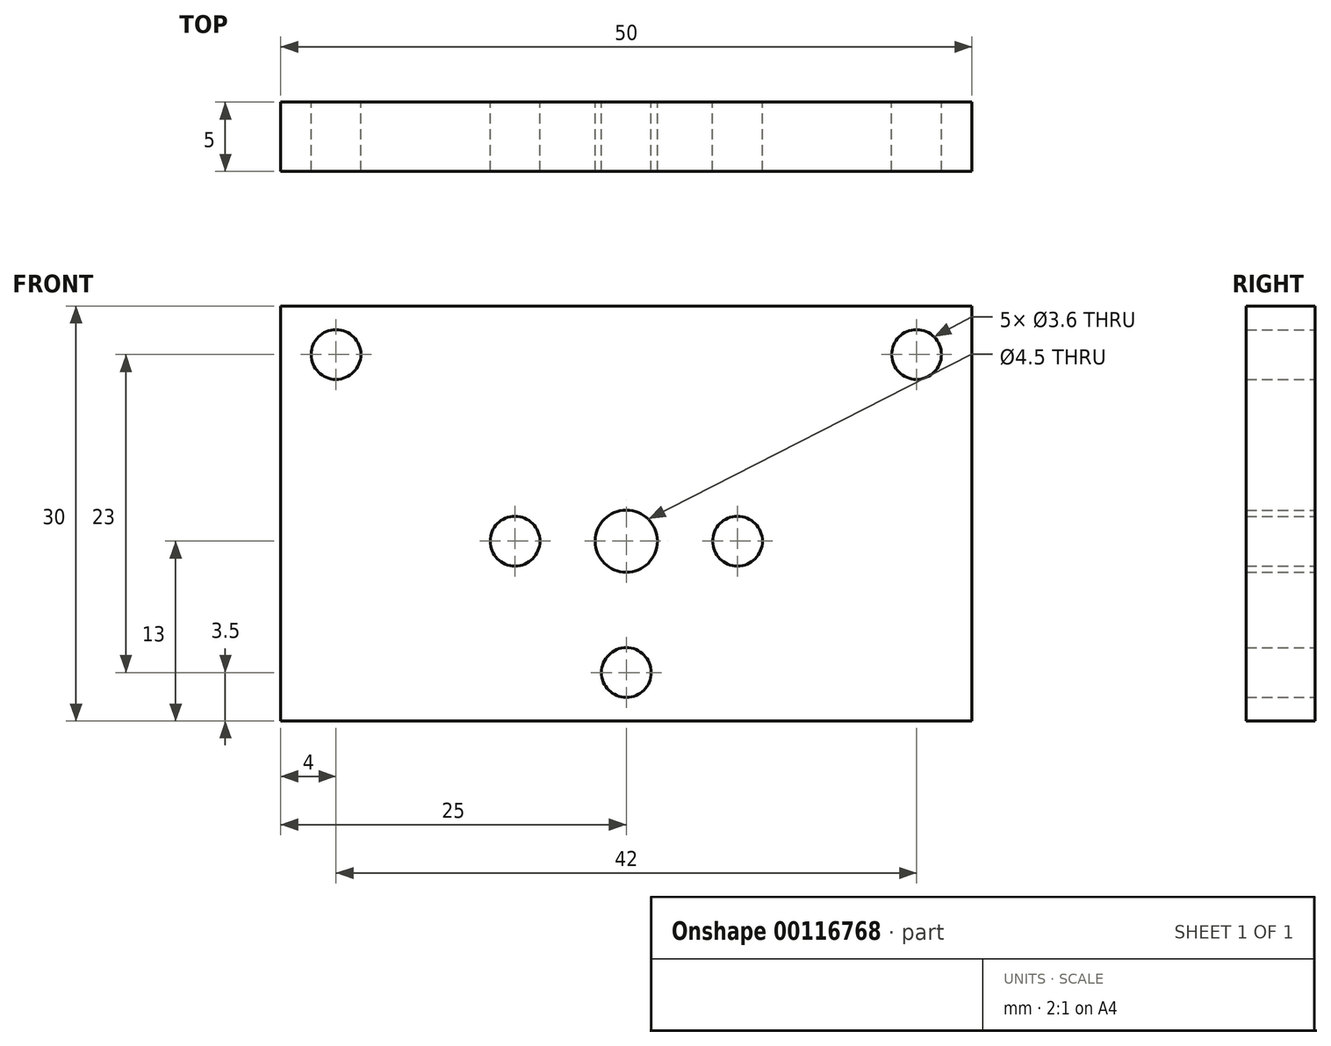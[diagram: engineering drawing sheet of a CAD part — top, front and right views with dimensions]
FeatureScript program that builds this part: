
annotation { "Feature Type Name" : "Feature", "Feature Type Description" : "" }
export const myFeature = defineFeature(function(context is Context, id is Id, definition is map)
    precondition{}
    {
        {
            var Q0;
            Q0=qCreatedBy(makeId("Front.planeOp"),FACE);
            var sketch = newSketch(context, id + "F0", { "sketchPlane" : qUnion([Q0])});
            skLineSegment(sketch, "E0.bottom", {"start": v(25, 15) * mm, "end": v(-25, 15) * mm});
            skLineSegment(sketch, "E0.top", {"start": v(25, -15) * mm, "end": v(-25, -15) * mm});
            skLineSegment(sketch, "E0.left", {"start": v(25, 15) * mm, "end": v(25, -15) * mm});
            skLineSegment(sketch, "E0.right", {"start": v(-25, 15) * mm, "end": v(-25, -15) * mm});
            skPoint(sketch, "E0.middle", {"position": v(0, 0) * mm});
            skSolve(sketch);
        }
        {
            var Q0;
            Q0=makeQuery(id+"F0.imprint","IMPRINT",FACE,{"disambiguationData":[TD([[makeQuery(id+"F0.imprint","IMPRINT",EDGE,{"derivedFrom":sQuery(id+"F0.wireOp",EDGE,"E0.bottom")}),1.0]])]});
            extrude(context, id + "F1", {"entities" : qUnion([Q0]), "depth" : 5 * mm});
        }
        {
            var Q0;
            Q0=makeQuery(id+"F1.opExtrude","CAP_FACE",FACE,{"disambiguationData":[OSD([sQuery(id+"F0.wireOp",EDGE,"E0.bottom"),sQuery(id+"F0.wireOp",EDGE,"E0.top"),sQuery(id+"F0.wireOp",EDGE,"E0.left"),sQuery(id+"F0.wireOp",EDGE,"E0.right")])],"isStart":true});
            var sketch = newSketch(context, id + "F2", { "sketchPlane" : qUnion([Q0])});
            skLineSegment(sketch, "E1", {"start": v(0, -15) * mm, "end": v(0, -11.5) * mm, "construction": true});
            skPoint(sketch, "E1.endSnap0", {"position": v(0, -15) * mm});
            skCircle(sketch, "E2", {"center": v(0, -11.5) * mm, "radius": 1.8 * mm});
            skSolve(sketch);
        }
        {
            var Q0;
            Q0 = qSketchRegion(id + "F2", true);
            extrude(context, id + "F3", {"entities" : qUnion([Q0]), "operationType" : NewBodyOperationType.REMOVE, "endBound" : BoundingType.THROUGH_ALL, "oppositeDirection" : true, "depth" : 25 * mm});
        }
        {
            var Q0;
            Q0=makeQuery(id+"F1.opExtrude","CAP_FACE",FACE,{"disambiguationData":[OSD([sQuery(id+"F0.wireOp",EDGE,"E0.bottom"),sQuery(id+"F0.wireOp",EDGE,"E0.top"),sQuery(id+"F0.wireOp",EDGE,"E0.left"),sQuery(id+"F0.wireOp",EDGE,"E0.right")])],"isStart":true});
            var sketch = newSketch(context, id + "F4", { "sketchPlane" : qUnion([Q0])});
            skLineSegment(sketch, "E3", {"start": v(0, -15) * mm, "end": v(0, -2) * mm, "construction": true});
            skPoint(sketch, "E3.endSnap0", {"position": v(0, -15) * mm});
            skLineSegment(sketch, "E4", {"start": v(0, -2) * mm, "end": v(8.05, -2) * mm, "construction": true});
            skCircle(sketch, "E5", {"center": v(8.05, -2) * mm, "radius": 1.8 * mm});
            skCircle(sketch, "E6", {"center": v(0, -2) * mm, "radius": 2.25 * mm});
            skCircle(sketch, "E7.MirrorC", {"center": v(-8.05, -2) * mm, "radius": 1.8 * mm});
            skSolve(sketch);
        }
        {
            var Q0;
            Q0 = qSketchRegion(id + "F4", true);
            extrude(context, id + "F5", {"entities" : qUnion([Q0]), "operationType" : NewBodyOperationType.REMOVE, "endBound" : BoundingType.THROUGH_ALL, "oppositeDirection" : true, "depth" : 25 * mm});
        }
        {
            var Q0;
            Q0=makeQuery(id+"F1.opExtrude","CAP_FACE",FACE,{"disambiguationData":[OSD([sQuery(id+"F0.wireOp",EDGE,"E0.bottom"),sQuery(id+"F0.wireOp",EDGE,"E0.top"),sQuery(id+"F0.wireOp",EDGE,"E0.left"),sQuery(id+"F0.wireOp",EDGE,"E0.right")])],"isStart":true});
            var sketch = newSketch(context, id + "F6", { "sketchPlane" : qUnion([Q0])});
            skLineSegment(sketch, "E8", {"start": v(-25, 15) * mm, "end": v(-21, 15) * mm, "construction": true});
            skLineSegment(sketch, "E9", {"start": v(-21, 15) * mm, "end": v(-21, 11.5) * mm, "construction": true});
            skCircle(sketch, "E10", {"center": v(-21, 11.5) * mm, "radius": 1.8 * mm});
            skCircle(sketch, "E11.MirrorC", {"center": v(21, 11.5) * mm, "radius": 1.8 * mm});
            skLineSegment(sketch, "E12.MirrorCS", {"start": v(21, 15) * mm, "end": v(21, 11.5) * mm, "construction": true});
            skSolve(sketch);
        }
        {
            var Q0;
            Q0 = qSketchRegion(id + "F6", true);
            extrude(context, id + "F7", {"entities" : qUnion([Q0]), "operationType" : NewBodyOperationType.REMOVE, "endBound" : BoundingType.THROUGH_ALL, "oppositeDirection" : true, "depth" : 25 * mm});
        }
    });
